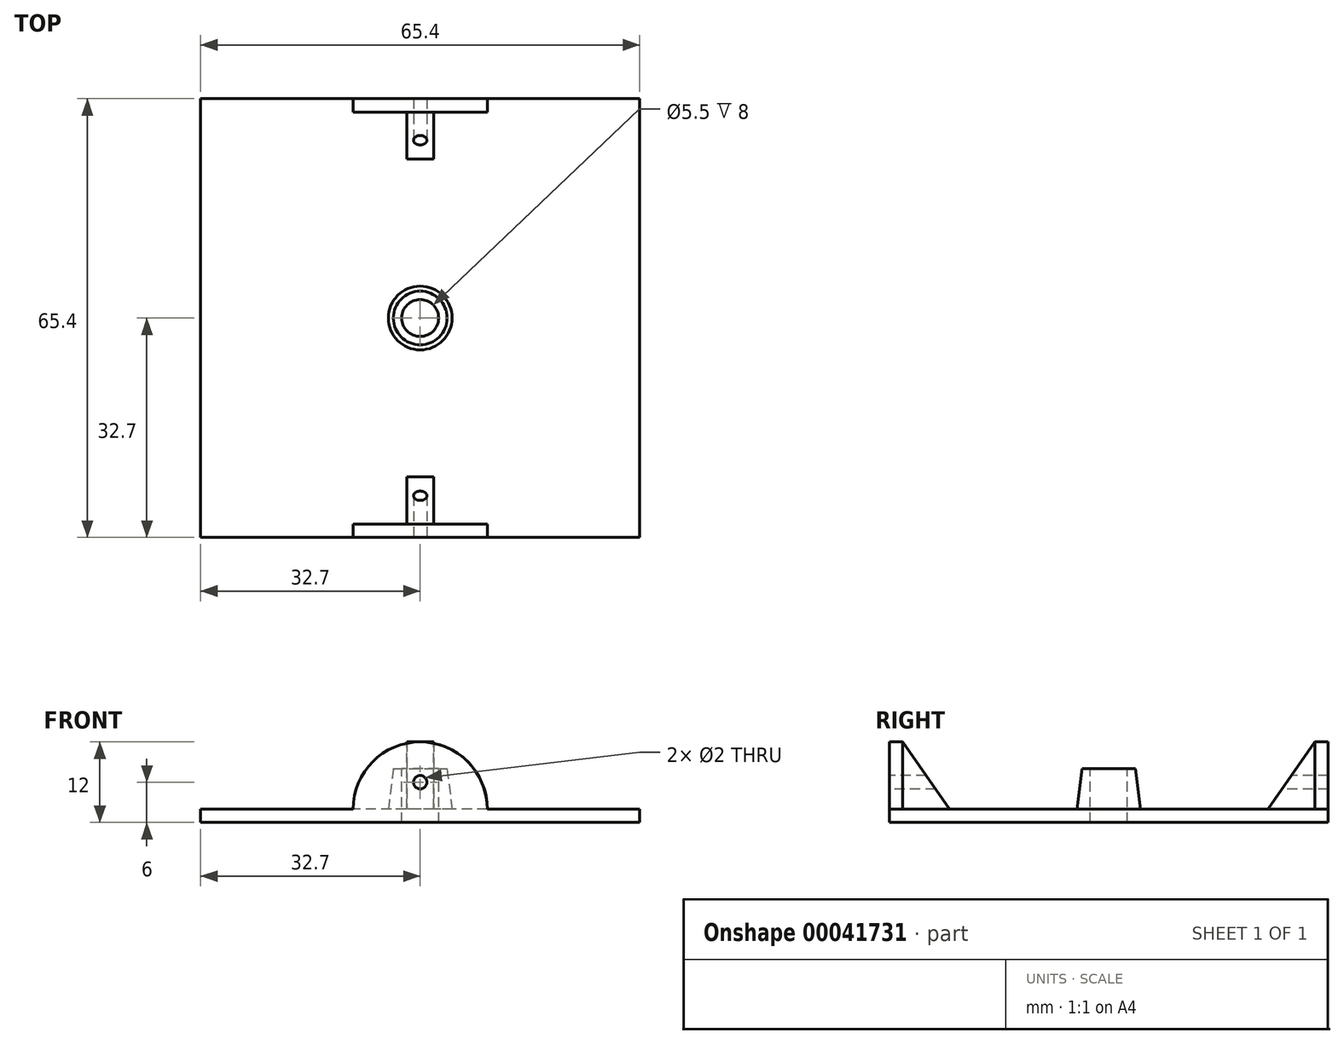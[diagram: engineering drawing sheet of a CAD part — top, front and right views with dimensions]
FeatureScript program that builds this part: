
annotation { "Feature Type Name" : "Feature", "Feature Type Description" : "" }
export const myFeature = defineFeature(function(context is Context, id is Id, definition is map)
    precondition{}
    {
        {
            var Q0;
            Q0=qCreatedBy(makeId("Top.planeOp"),FACE);
            var sketch = newSketch(context, id + "F0", { "sketchPlane" : qUnion([Q0])});
            skLineSegment(sketch, "E0.rect.bottom", {"start": v(32.7, 32.7) * mm, "end": v(-32.7, 32.7) * mm});
            skLineSegment(sketch, "E0.rect.top", {"start": v(32.7, -32.7) * mm, "end": v(-32.7, -32.7) * mm});
            skLineSegment(sketch, "E0.rect.left", {"start": v(32.7, 32.7) * mm, "end": v(32.7, -32.7) * mm});
            skLineSegment(sketch, "E0.rect.right", {"start": v(-32.7, 32.7) * mm, "end": v(-32.7, -32.7) * mm});
            skPoint(sketch, "E0.rect.middle", {"position": v(0, 0) * mm});
            skSolve(sketch);
        }
        {
            var Q0;
            Q0=qSketchRegion(id+"F0",true);
            extrude(context, id + "F1", {"entities" : qUnion([Q0]), "depth" : 2 * mm});
        }
        {
            var Q0;
            Q0=makeQuery(id+"F1.opExtrude","SWEPT_FACE",FACE,{"disambiguationData":[OSD([sQuery(id+"F0.wireOp",EDGE,"E0.rect.top")])]});
            var sketch = newSketch(context, id + "F2", { "sketchPlane" : qUnion([Q0])});
            skLineSegment(sketch, "E1", {"start": v(0, 2) * mm, "end": v(10, 2) * mm});
            skLineSegment(sketch, "E2", {"start": v(0, 2) * mm, "end": v(-10, 2) * mm});
            skArc(sketch, "E3", {"start": v(10, 2) * mm, "mid": v(0, 12) * mm, "end": v(-10, 2) * mm});
            skSolve(sketch);
        }
        {
            var Q0;
            Q0=qSketchRegion(id+"F2",true);
            extrude(context, id + "F3", {"entities" : qUnion([Q0]), "operationType" : NewBodyOperationType.ADD, "oppositeDirection" : true, "depth" : 2 * mm});
        }
        {
            var Q0;
            Q0=makeQuery(id+"F1.opExtrude","SWEPT_FACE",FACE,{"disambiguationData":[OSD([sQuery(id+"F0.wireOp",EDGE,"E0.rect.bottom")])]});
            var sketch = newSketch(context, id + "F4", { "sketchPlane" : qUnion([Q0])});
            skLineSegment(sketch, "E4", {"start": v(0, 2) * mm, "end": v(10, 2) * mm});
            skLineSegment(sketch, "E5", {"start": v(0, 2) * mm, "end": v(-10, 2) * mm});
            skArc(sketch, "E6", {"start": v(10, 2) * mm, "mid": v(0, 12) * mm, "end": v(-10, 2) * mm});
            skSolve(sketch);
        }
        {
            var Q0;
            Q0=qSketchRegion(id+"F4",true);
            extrude(context, id + "F5", {"entities" : qUnion([Q0]), "operationType" : NewBodyOperationType.ADD, "oppositeDirection" : true, "depth" : 2 * mm});
        }
        {
            var Q0;
            Q0=qCreatedBy(makeId("Right.planeOp"),FACE);
            var sketch = newSketch(context, id + "F6", { "sketchPlane" : qUnion([Q0])});
            skPoint(sketch, "E7.0", {"position": v(30.7, 2) * mm});
            skLineSegment(sketch, "E8", {"start": v(30.7, 2) * mm, "end": v(30.7, 12) * mm});
            skLineSegment(sketch, "E9", {"start": v(30.7, 2) * mm, "end": v(23.7, 2) * mm});
            skLineSegment(sketch, "E10", {"start": v(30.7, 12) * mm, "end": v(23.7, 2) * mm});
            skLineSegment(sketch, "E11", {"start": v(0, 0) * mm, "end": v(0, 11.7) * mm});
            skLineSegment(sketch, "E12.MirrorCS", {"start": v(-30.7, 12) * mm, "end": v(-23.7, 2) * mm});
            skLineSegment(sketch, "E13.MirrorCS", {"start": v(-30.7, 2) * mm, "end": v(-30.7, 12) * mm});
            skLineSegment(sketch, "E14.MirrorCS", {"start": v(-30.7, 2) * mm, "end": v(-23.7, 2) * mm});
            skSolve(sketch);
        }
        {
            var Q0;
            Q0=qSketchRegion(id+"F6",true);
            extrude(context, id + "F7", {"entities" : qUnion([Q0]), "operationType" : NewBodyOperationType.ADD, "depth" : 2 * mm, "hasSecondDirection" : true, "secondDirectionOppositeDirection" : true, "secondDirectionDepth" : 2 * mm});
        }
        {
            var Q0;
            Q0=makeQuery(id+"F3.boolean.opBoolean","MERGE",FACE,{"derivedFrom":[makeQuery(id+"F1.opExtrude","SWEPT_FACE",FACE,{"disambiguationData":[OSD([sQuery(id+"F0.wireOp",EDGE,"E0.rect.top")])]}),makeQuery(id+"F3.opExtrude","CAP_FACE",FACE,{"disambiguationData":[OSD([sQuery(id+"F2.wireOp",EDGE,"E1"),sQuery(id+"F2.wireOp",EDGE,"E2"),sQuery(id+"F2.wireOp",EDGE,"E3")])],"isStart":true})]});
            var sketch = newSketch(context, id + "F8", { "sketchPlane" : qUnion([Q0])});
            skLineSegment(sketch, "E15", {"start": v(0, 0) * mm, "end": v(0, 6) * mm});
            skCircle(sketch, "E16", {"center": v(0, 6) * mm, "radius": 1 * mm});
            skSolve(sketch);
        }
        {
            var Q0;
            Q0=qSketchRegion(id+"F8",true);
            extrude(context, id + "F9", {"entities" : qUnion([Q0]), "operationType" : NewBodyOperationType.REMOVE, "endBound" : BoundingType.THROUGH_ALL, "oppositeDirection" : true, "depth" : 25 * mm});
        }
        {
            var Q0;
            Q0=qCreatedBy(makeId("Front.planeOp"),FACE);
            var sketch = newSketch(context, id + "F10", { "sketchPlane" : qUnion([Q0])});
            skLineSegment(sketch, "E17", {"start": v(0, 0) * mm, "end": v(0, 8) * mm});
            skLineSegment(sketch, "E18", {"start": v(0, 8) * mm, "end": v(4, 8) * mm});
            skLineSegment(sketch, "E19", {"start": v(4, 8) * mm, "end": v(5, 0) * mm});
            skLineSegment(sketch, "E20", {"start": v(5, 0) * mm, "end": v(0, 0) * mm});
            skSolve(sketch);
        }
        {
            var Q0;
            Q0=qSketchRegion(id+"F10",true);
            var Q1;
            Q1=sQuery(id+"F10.wireOp",EDGE,"E17");
            revolve(context, id + "F11", {"operationType" : NewBodyOperationType.ADD, "entities" : qUnion([Q0]), "axis" : qUnion([Q1]), "revolveType" : RevolveType.FULL});
        }
        {
            var Q0;
            Q0=makeQuery(id+"F11.opRevolve","SWEPT_FACE",FACE,{"disambiguationData":[OSD([sQuery(id+"F10.wireOp",EDGE,"E18")])]});
            var sketch = newSketch(context, id + "F12", { "sketchPlane" : qUnion([Q0])});
            skCircle(sketch, "E21", {"center": v(0, 0) * mm, "radius": 2.75 * mm});
            skSolve(sketch);
        }
        {
            var Q0;
            Q0=qSketchRegion(id+"F12",true);
            extrude(context, id + "F13", {"entities" : qUnion([Q0]), "operationType" : NewBodyOperationType.REMOVE, "endBound" : BoundingType.THROUGH_ALL, "oppositeDirection" : true, "depth" : 25 * mm});
        }
    });
